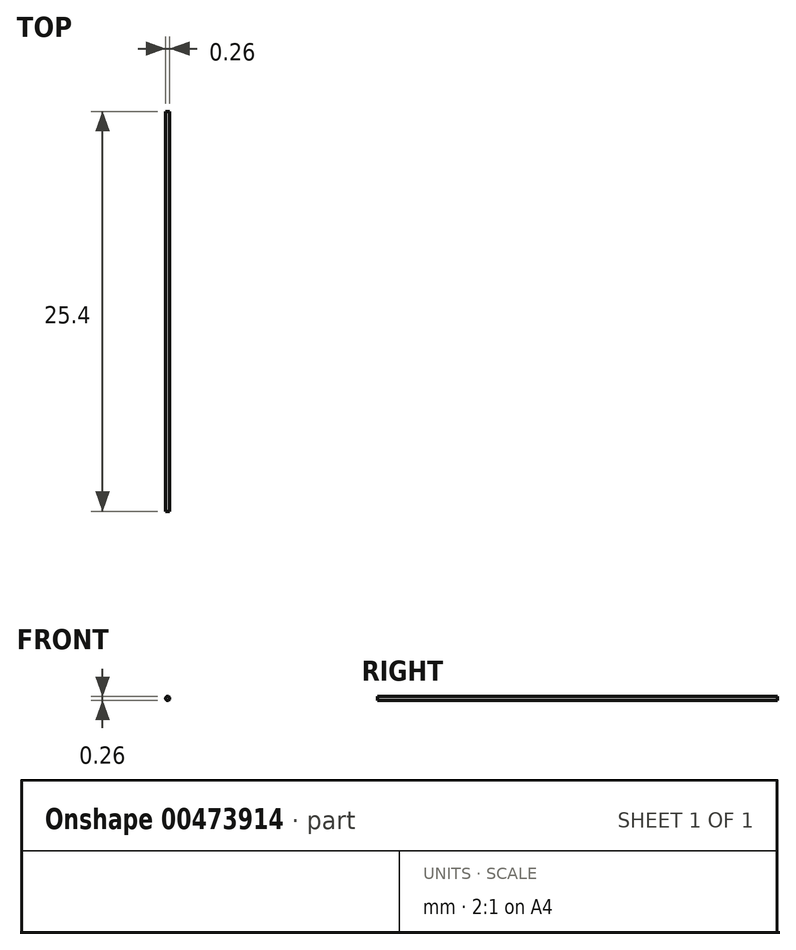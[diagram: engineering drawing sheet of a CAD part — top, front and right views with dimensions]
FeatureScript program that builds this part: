
annotation { "Feature Type Name" : "Feature", "Feature Type Description" : "" }
export const myFeature = defineFeature(function(context is Context, id is Id, definition is map)
    precondition{}
    {
        {
            var Q0;
            Q0=qCreatedBy(makeId("Front.planeOp"),FACE);
            var sketch = newSketch(context, id + "F0", { "sketchPlane" : qUnion([Q0])});
            skCircle(sketch, "E0", {"center": v(0, 0) * mm, "radius": 0.13 * mm});
            skSolve(sketch);
        }
        {
            var Q0;
            Q0 = qSketchRegion(id + "F0", true);
            extrude(context, id + "F1", {"entities" : qUnion([Q0]), "depth" : 25.4 * mm});
        }
    });
